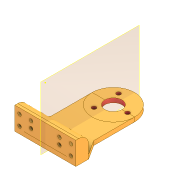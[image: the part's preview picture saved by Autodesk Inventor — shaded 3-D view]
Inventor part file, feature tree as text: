
AUTODESK INVENTOR PART (.ipt)
format: ipt  version: 2020.3 (Build 243373000, 373)  size: 205,312 bytes
history: native  units: mm
features: sketch x6, extrude x5, direct_edit x1, plane x1, imported_body x1, move_body x1
ambient origin geometry x8: Origin, YZ Plane, XZ Plane, XY Plane, X Axis, Y Axis, Z Axis, Center Point
bodies: Solid1 (feature_tree)
feature tree (15):
  direct_edit  "Direct Edit1"
  extrude  "Extrusion1"  Depth=10.0mm
  sketch  "Sketch2"  dims[d4=7.0mm d5=10.0mm d6=0.0mm]
  sketch  "Sketch3"  dims[d7=2.5mm d8=2.5mm]
  extrude  "Extrusion2"  Depth=10.0mm TaperAngle=0.0deg
  plane  "Work Plane1"
  extrude  "Extrusion4"  Depth=2.5mm
  extrude  "Extrusion3"  Depth=9.0mm
  extrude  "Extrusion6"  Depth=7.0mm
  sketch  "Sketch1"  dims[d0=0.0mm d1=0.0mm d2=-7.0mm d3=10.0mm]
  sketch  "Sketch4"  dims[d9=16.0mm d10=9.0mm]
  sketch  "Sketch5"  dims[d11=7.0mm d12=2.5mm]
  sketch  "Sketch7"  dims[d13=2.5mm d15=29.0mm d16=0.0mm d17=10.0mm d18=0.0mm d19=43.0mm d20=0.0mm d23=2.5mm d24=2.5mm d25=36.319mm d26=2.5mm d27=2.5mm d32=12.0mm d33=12.0mm d34=2.75mm d35=0.0mm d36=4.86mm d37=7.356mm]
  imported_body  "Base1"
  move_body  "Move1"
